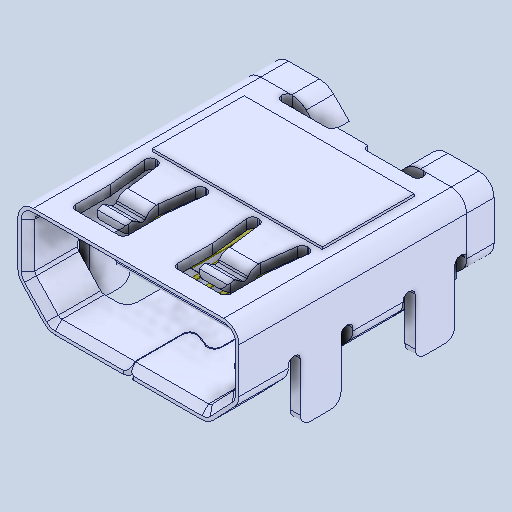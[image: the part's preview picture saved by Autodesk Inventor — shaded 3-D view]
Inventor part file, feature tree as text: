
AUTODESK INVENTOR PART (.ipt)
format: ipt  version: 2022 (Build 260153000, 153)  size: 1,056,768 bytes
history: mixed  units: in
note: dims shown in document units (in); Inventor stores cm internally (conversion verified against a paired STEP export)
features: other x40, chamfer x3, fillet x1, imported_body x1
ambient origin geometry x8: Origin, YZ Plane, XZ Plane, XY Plane, X Axis, Y Axis, Z Axis, Center Point
bodies: Solid1 (imported_parasolid), Solid2 (imported_parasolid), Solid3 (imported_parasolid), Solid4 (imported_parasolid), Solid5 (imported_parasolid), Solid6 (imported_parasolid), Solid7 (imported_parasolid), Solid8 (imported_parasolid), Solid9 (imported_parasolid), Solid10 (imported_parasolid), Solid11 (imported_parasolid), Solid12 (imported_parasolid), Solid13 (imported_parasolid), Solid14 (imported_parasolid), Solid15 (imported_parasolid), Solid16 (imported_parasolid), Solid17 (imported_parasolid), Solid18 (imported_parasolid), Solid19 (imported_parasolid), Solid20 (imported_parasolid), Solid21 (imported_parasolid), Solid22 (imported_parasolid), Solid23 (imported_parasolid), Solid24 (imported_parasolid), Solid25 (imported_parasolid), Solid26 (imported_parasolid), Solid27 (imported_parasolid), Solid28 (imported_parasolid), Solid29 (imported_parasolid), Solid30 (imported_parasolid), Solid31 (imported_parasolid), Solid32 (imported_parasolid), Solid33 (imported_parasolid), Solid34 (imported_parasolid), Solid35 (imported_parasolid), Solid36 (imported_parasolid), Solid37 (imported_parasolid), Solid38 (imported_parasolid), Solid39 (imported_parasolid), Solid40 (imported_parasolid), Solid41 (imported_parasolid), Solid42 (imported_parasolid), Solid43 (imported_parasolid), Solid44 (imported_parasolid)
feature tree (45):
  other  "Cut-Extrude2"
  fillet  "Fillet2"  [1 undecoded]
  other  "LPattern1[1]"
  other  "LPattern1[2]"
  other  "LPattern1[3]"
  other  "LPattern1[4]"
  other  "LPattern1[5]"
  other  "LPattern1[6]"
  other  "LPattern1[7]"
  other  "LPattern1[8]"
  other  "LPattern1[9]"
  other  "Boss-Extrude4"
  other  "LPattern2[1]"
  other  "LPattern2[2]"
  other  "LPattern2[3]"
  other  "LPattern2[4]"
  other  "LPattern2[5]"
  other  "LPattern2[6]"
  other  "LPattern2[7]"
  other  "LPattern2[8]"
  other  "LPattern3[1]"
  other  "LPattern3[2]"
  other  "LPattern3[3]"
  other  "LPattern3[4]"
  other  "LPattern3[5]"
  other  "LPattern3[6]"
  other  "LPattern3[7]"
  other  "LPattern3[8]"
  other  "Boss-Extrude9"
  other  "LPattern4[1]"
  other  "LPattern4[2]"
  other  "LPattern4[3]"
  other  "LPattern4[4]"
  other  "LPattern4[5]"
  other  "LPattern4[6]"
  other  "LPattern4[7]"
  other  "LPattern4[8]"
  other  "Cut-Extrude13[1]"
  other  "Cut-Extrude13[2]"
  other  "Boss-Extrude15[2]"
  other  "Cut-Extrude18[3]"
  chamfer  "Chamfer5"  [1 undecoded]
  chamfer  "Chamfer6"  [1 undecoded]
  chamfer  "Chamfer7"  [1 undecoded]
  imported_body  NMx_Import_Brep_tag  [imported B-rep: ~222 faces, bbox_mm=[0.0, 0.0, 0.36]]
note: 4 required parameter values undecoded (feature->parameter linkage not recoverable at this tier; creation-order binding heuristic only, values carry confidence <= 0.55)
